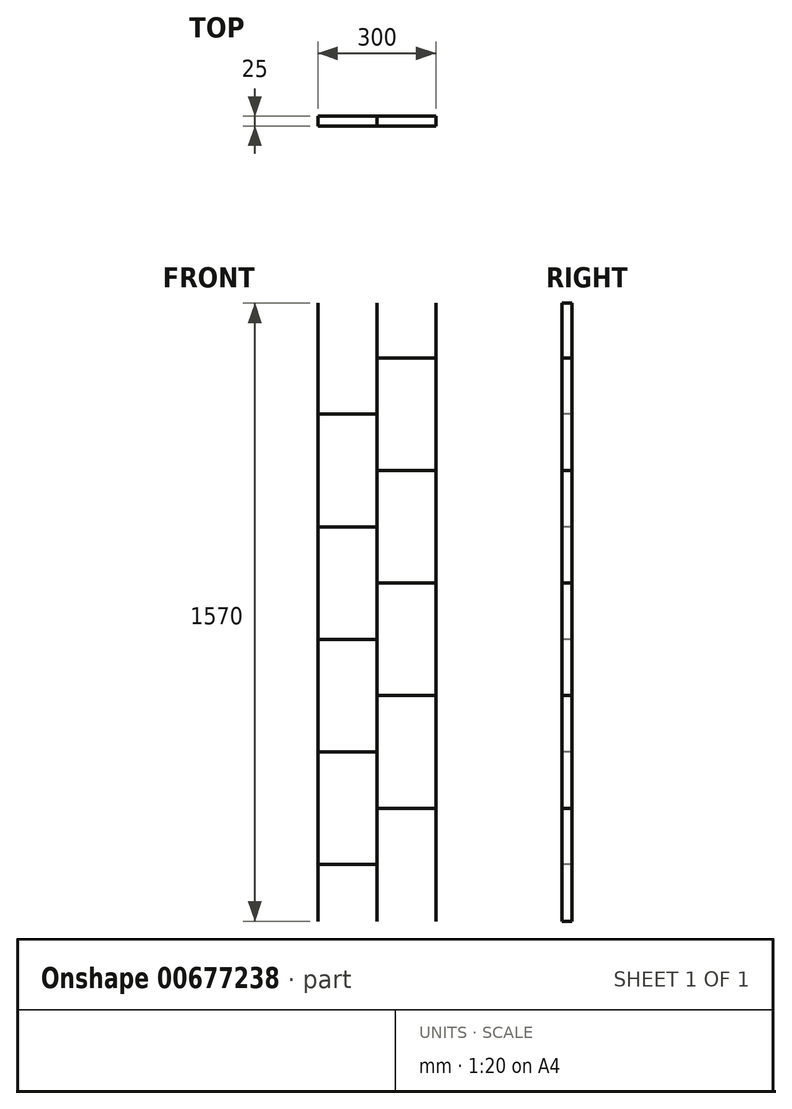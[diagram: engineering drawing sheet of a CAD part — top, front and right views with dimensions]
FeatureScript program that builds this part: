
annotation { "Feature Type Name" : "Feature", "Feature Type Description" : "" }
export const myFeature = defineFeature(function(context is Context, id is Id, definition is map)
    precondition{}
    {
        {
            var Q0;
            Q0=qCreatedBy(makeId("Front.planeOp"),FACE);
            var sketch = newSketch(context, id + "F0", { "sketchPlane" : qUnion([Q0])});
            skLineSegment(sketch, "E0.top", {"start": v(-250, -930.32) * mm, "end": v(250, -930.32) * mm});
            skLineSegment(sketch, "E0.left", {"start": v(-250, 639.68) * mm, "end": v(-250, -930.32) * mm});
            skLineSegment(sketch, "E0.right", {"start": v(250, 639.68) * mm, "end": v(250, -930.32) * mm});
            skLineSegment(sketch, "E1", {"start": v(-150, 639.68) * mm, "end": v(-150, -930.32) * mm});
            skLineSegment(sketch, "E2", {"start": v(0, 639.68) * mm, "end": v(0, -930.32) * mm});
            skLineSegment(sketch, "E3", {"start": v(150, 639.68) * mm, "end": v(150, -930.32) * mm});
            skLineSegment(sketch, "E4", {"start": v(150, 500.68) * mm, "end": v(0, 500.68) * mm});
            skLineSegment(sketch, "E5", {"start": v(150, 214.68) * mm, "end": v(0, 214.68) * mm});
            skLineSegment(sketch, "E6", {"start": v(150, -71.32) * mm, "end": v(0, -71.32) * mm});
            skLineSegment(sketch, "E7", {"start": v(150, -357.32) * mm, "end": v(0, -357.32) * mm});
            skLineSegment(sketch, "E8", {"start": v(150, -643.32) * mm, "end": v(0, -643.32) * mm});
            skLineSegment(sketch, "E9", {"start": v(-150, -786.32) * mm, "end": v(0, -786.32) * mm});
            skLineSegment(sketch, "E10", {"start": v(-150, -500.32) * mm, "end": v(0, -500.32) * mm});
            skLineSegment(sketch, "E11", {"start": v(-150, -214.32) * mm, "end": v(0, -214.32) * mm});
            skLineSegment(sketch, "E12", {"start": v(-150, 71.68) * mm, "end": v(0, 71.68) * mm});
            skLineSegment(sketch, "E13", {"start": v(-150, 357.68) * mm, "end": v(0, 357.68) * mm});
            skLineSegment(sketch, "E14", {"start": v(-250, 639.68) * mm, "end": v(250, 639.68) * mm});
            skSolve(sketch);
        }
        {
            var Q0;
            Q0=sQuery(id+"F0.wireOp",EDGE,"E13");
            var Q1;
            Q1=sQuery(id+"F0.wireOp",EDGE,"E12");
            var Q2;
            Q2=sQuery(id+"F0.wireOp",EDGE,"E11");
            var Q3;
            Q3=sQuery(id+"F0.wireOp",EDGE,"E10");
            var Q4;
            Q4=sQuery(id+"F0.wireOp",EDGE,"E9");
            var Q5;
            Q5=sQuery(id+"F0.wireOp",EDGE,"E8");
            var Q6;
            Q6=sQuery(id+"F0.wireOp",EDGE,"E7");
            var Q7;
            Q7=sQuery(id+"F0.wireOp",EDGE,"E6");
            var Q8;
            Q8=sQuery(id+"F0.wireOp",EDGE,"E5");
            var Q9;
            Q9=sQuery(id+"F0.wireOp",EDGE,"E4");
            extrude(context, id + "F1", {"bodyType" : ToolBodyType.SURFACE, "surfaceEntities" : qUnion([Q0, Q1, Q2, Q3, Q4, Q5, Q6, Q7, Q8, Q9]), "depth" : 25 * mm, "offsetDistance" : 25 * mm});
        }
        {
            var Q0;
            Q0=sQuery(id+"F0.wireOp",EDGE,"E3");
            var Q1;
            Q1=sQuery(id+"F0.wireOp",EDGE,"E2");
            var Q2;
            Q2=sQuery(id+"F0.wireOp",EDGE,"E1");
            extrude(context, id + "F2", {"bodyType" : ToolBodyType.SURFACE, "surfaceEntities" : qUnion([Q0, Q1, Q2]), "depth" : 25 * mm, "offsetDistance" : 25 * mm});
        }
    });
